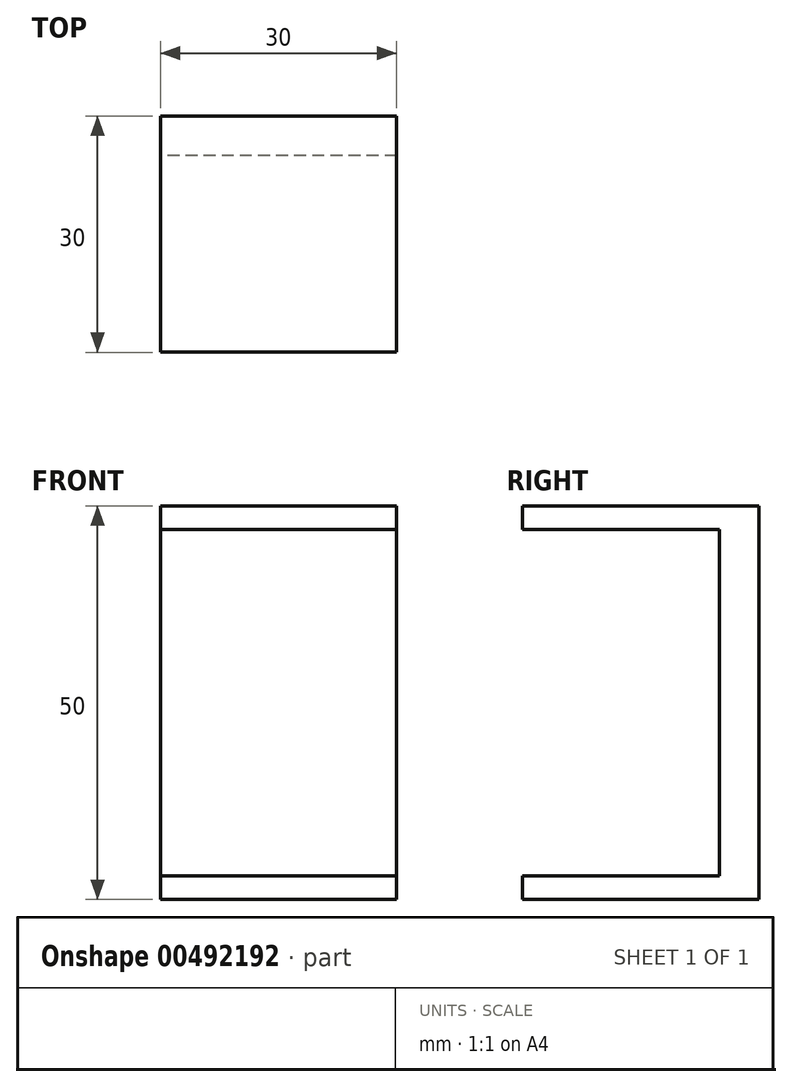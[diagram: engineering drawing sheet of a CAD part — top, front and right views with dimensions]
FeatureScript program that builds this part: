
annotation { "Feature Type Name" : "Feature", "Feature Type Description" : "" }
export const myFeature = defineFeature(function(context is Context, id is Id, definition is map)
    precondition{}
    {
        {
            var Q0;
            Q0=qCreatedBy(makeId("Right.planeOp"),FACE);
            var sketch = newSketch(context, id + "F0", { "sketchPlane" : qUnion([Q0])});
            skLineSegment(sketch, "E0", {"start": v(-30, -1.87) * mm, "end": v(0, -1.87) * mm});
            skLineSegment(sketch, "E1", {"start": v(0, -1.87) * mm, "end": v(0, -51.87) * mm});
            skLineSegment(sketch, "E2", {"start": v(0, -51.87) * mm, "end": v(-30, -51.87) * mm});
            skLineSegment(sketch, "E3", {"start": v(-30, -51.87) * mm, "end": v(-30, -48.87) * mm});
            skLineSegment(sketch, "E4", {"start": v(-30, -48.87) * mm, "end": v(-5, -48.87) * mm});
            skLineSegment(sketch, "E5", {"start": v(-5, -48.87) * mm, "end": v(-5, -4.87) * mm});
            skLineSegment(sketch, "E6", {"start": v(-5, -4.87) * mm, "end": v(-30, -4.87) * mm});
            skLineSegment(sketch, "E7", {"start": v(-30, -4.87) * mm, "end": v(-30, -1.87) * mm});
            skSolve(sketch);
        }
        {
            var Q0;
            Q0=makeQuery(id+"F0.imprint","IMPRINT",FACE,{"disambiguationData":[TD([[makeQuery(id+"F0.imprint","IMPRINT",EDGE,{"derivedFrom":sQuery(id+"F0.wireOp",EDGE,"E0")}),-1.0]])]});
            extrude(context, id + "F1", {"entities" : qUnion([Q0]), "depth" : 30 * mm, "symmetric" : true});
        }
        {
            var Q0;
            Q0=makeQuery(id+"F1.opExtrude","SWEPT_BODY",BODY,{"disambiguationData":[OSD([sQuery(id+"F0.wireOp",EDGE,"E0"),sQuery(id+"F0.wireOp",EDGE,"E1"),sQuery(id+"F0.wireOp",EDGE,"E2"),sQuery(id+"F0.wireOp",EDGE,"E3"),sQuery(id+"F0.wireOp",EDGE,"E4"),sQuery(id+"F0.wireOp",EDGE,"E5"),sQuery(id+"F0.wireOp",EDGE,"E6"),sQuery(id+"F0.wireOp",EDGE,"E7")])]});
            transform(context, id + "F2", {"entities" : qUnion([Q0]), "transformType" : TransformType.TRANSLATION_3D, "dx" : 0 * mm, "dy" : 3.7 * mm, "dz" : 28.47 * mm, "makeCopy" : false});
        }
    });
